# Revit family: FaEl_Compact_Interior
name_source: partatom
category: Fassadenelemente
units: mm (PartAtom-declared; Revit-internal decimal feet)

## family parameters
Beim Laden mit Abzugskörper schneiden = Nein
Gemeinsam genutzt = Nein
Immer vertikal = Ja
OmniClass-Nummer = 23.25.00.00
OmniClass-Titel = Structural and Space Division Products

## types (15) — shared parameters
Analytische Konstruktion = <Keine Auswahl>
Apparent_Density = 1.35 g/cm³
AssetType = Fixed
Certification = CE- marked, BBA 12/4937
Combustible = Nein
Core = Black core
Duration_Unit = year
Features = Graffitti-resistant, weather-resistant, flame-retardant core, lightfast, double-hardened, scratch and solvent resistant, easy to clean, custom shapes also available
Finish_Options = Slabs, triangle, cone, bowl, wave small grey, wave gold large, naturell, letter, bubble, knitter
FireRating = Euroclass B-s2, d0
Flexural_Strength = ≥ 90 MPa
Grade = To BS EN 438-6, Type EDF
IfcExportAs = IfcCoveringType
IfcExportType = NOTDEFINED
IsExternal = Ja
Manufacturer_Name = FunderMax GmbH
Manufacturer_URL = http://www.fundermax.at
Modulus_Of-Elasticity = ≥ 9.0 MPa
Panel_Material = FunderMax_Compact_Resistance
Product_Information = https://www.ribaproductselector.com
Shape = Rectangle
Surface = NT
Tensile_Strength = ≥ 80 MPa
Thermal_Conductivity = 0.3 W/mK
Thermal_Expansion_Coefficient = 18x10^-6 1/K
Tolerances = 0,2mm
Version = 3
Warranty_Duration_Unit = year
Water_Vapour_Diffusion_Resistance = 17.200 μ

## per-type parameters (varying)
| type | Panel_Size_Length | Panel_Size_Width | Panel_Thickness | Size | Thickness_Options |
| 2140x1060x0010 | 2140 | 1060 | 10 mm  [stored 0.0328084 ft] | 2140x1060x0010 | 2-20mm |
| 2140x1060x0002 | 2140 | 1060 | 2 mm  [stored 0.00656168 ft] | 2140x1060x0002 | 2-20mm |
| 2140x1600x0020 | 2140 | 1060 | 20 mm  [stored 0.0656168 ft] | 2140x1060x0020 | 2-20mm |
| 2800x1300x0002 | 2800 | 1300 | 2 mm  [stored 0.00656168 ft] | 2800x1300x0002 | 2-20mm |
| 2800x1300x0010 | 2800 | 1300 | 10 mm  [stored 0.0328084 ft] | 2800x1300x0010 | 2-20mm |
| 2800x1300x0020 | 2800 | 1300 | 20 mm  [stored 0.0656168 ft] | 2800x1300x0020 | 2-20mm |
| 2800x1854x0002 | 2800 | 1854 | 2 mm  [stored 0.00656168 ft] | 2800x1854x0002 | 2-15mm |
| 2800x1854x0010 | 2800 | 1854 | 10 mm  [stored 0.0328084 ft] | 2800x1854x0010 | 2-15mm |
| 2800x1854x0015 | 2800 | 1854 | 15 mm | 2800x1854x0015 | 2-15mm |
| 4100x1300x0002 | 4100 | 13000 | 2 mm  [stored 0.00656168 ft] | 4100x1300x0002 | 2-20mm |
| 4100x1300x0010 | 4100 | 13000 | 10 mm  [stored 0.0328084 ft] | 4100x1300x0010 | 2-20mm |
| 4100x1300x0020 | 4100 | 13000 | 20 mm  [stored 0.0656168 ft] | 4100x1300x0020 | 2-20mm |
| 4100x1854x0002 | 4100 | 1854 | 2 mm  [stored 0.00656168 ft] | 4100x1854x0002 | 2-20mm |
| 4100x1854x0010 | 4100 | 1854 | 10 mm  [stored 0.0328084 ft] | 4100x1854x0010 | 2-20mm |
| 4100x1854x0020 | 4100 | 1854 | 20 mm  [stored 0.0656168 ft] | 4100x1854x0020 | 2-20mm |

note: [stored X ft] marks values corroborated as IEEE doubles in the binary element streams (Revit-internal decimal feet)
